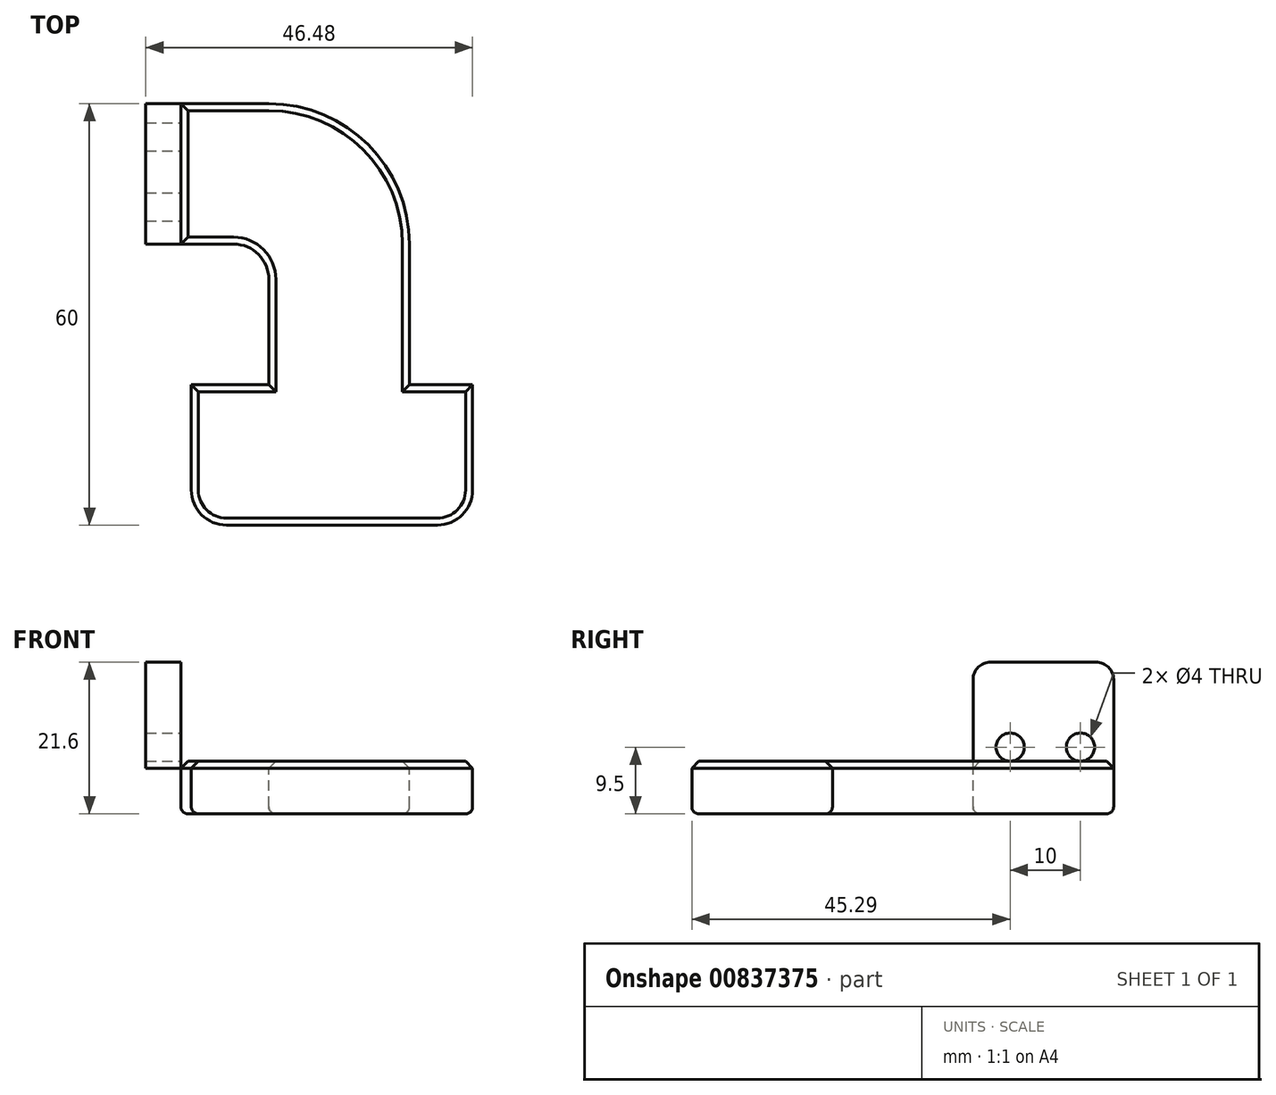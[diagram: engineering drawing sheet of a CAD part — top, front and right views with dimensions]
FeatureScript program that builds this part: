
annotation { "Feature Type Name" : "Feature", "Feature Type Description" : "" }
export const myFeature = defineFeature(function(context is Context, id is Id, definition is map)
    precondition{}
    {
        {
            var Q0;
            Q0=qCreatedBy(makeId("Top.planeOp"),FACE);
            var sketch = newSketch(context, id + "F0", { "sketchPlane" : qUnion([Q0])});
            skLineSegment(sketch, "E0.bottom", {"start": v(-27.76, 10) * mm, "end": v(-15.26, 10) * mm});
            skLineSegment(sketch, "E0.top", {"start": v(-27.76, -10) * mm, "end": v(-20.26, -10) * mm});
            skLineSegment(sketch, "E1.top", {"start": v(4.74, -30) * mm, "end": v(-15.26, -30) * mm});
            skLineSegment(sketch, "E1.left", {"start": v(4.74, -10) * mm, "end": v(4.74, -30) * mm});
            skLineSegment(sketch, "E1.right", {"start": v(-15.26, -15) * mm, "end": v(-15.26, -30) * mm});
            skLineSegment(sketch, "E2.bottom", {"start": v(13.72, -30) * mm, "end": v(-26.28, -30) * mm});
            skLineSegment(sketch, "E2.top", {"start": v(8.72, -50) * mm, "end": v(-21.28, -50) * mm});
            skLineSegment(sketch, "E2.left", {"start": v(13.72, -30) * mm, "end": v(13.72, -45) * mm});
            skLineSegment(sketch, "E2.right", {"start": v(-26.28, -30) * mm, "end": v(-26.28, -45) * mm});
            skPoint(sketch, "E3.visualSharp", {"position": v(4.74, 10) * mm});
            skArc(sketch, "E3.filletArc", {"start": v(4.74, -10) * mm, "mid": v(-1.12, 4.14) * mm, "end": v(-15.26, 10) * mm});
            skArc(sketch, "E4.filletArc", {"start": v(-15.26, -15) * mm, "mid": v(-16.72, -11.46) * mm, "end": v(-20.26, -10) * mm});
            skPoint(sketch, "E5.visualSharp", {"position": v(13.72, -50) * mm});
            skArc(sketch, "E5.filletArc", {"start": v(8.72, -50) * mm, "mid": v(12.26, -48.54) * mm, "end": v(13.72, -45) * mm});
            skPoint(sketch, "E6.visualSharp", {"position": v(-26.28, -50) * mm});
            skArc(sketch, "E6.filletArc", {"start": v(-26.28, -45) * mm, "mid": v(-24.81, -48.54) * mm, "end": v(-21.28, -50) * mm});
            skLineSegment(sketch, "E7.left", {"start": v(-27.76, 10) * mm, "end": v(-27.76, -10) * mm});
            skPoint(sketch, "E8.center.orphan", {"position": v(-40.26, 0) * mm});
            skPoint(sketch, "E9.orphan", {"position": v(-52.17, -10) * mm});
            skPoint(sketch, "E10.orphan", {"position": v(-40.26, 10) * mm});
            skPoint(sketch, "E11.orphan", {"position": v(-40.26, -10) * mm});
            skSolve(sketch);
        }
        {
            var Q0;
            Q0=makeQuery(id+"F0.imprint","IMPRINT",FACE,{"disambiguationData":[TD([[makeQuery(id+"F0.imprint","IMPRINT",EDGE,{"derivedFrom":sQuery(id+"F0.wireOp",EDGE,"E8")}),-1.0]])]});
            var Q1;
            Q1=makeQuery(id+"F0.imprint","IMPRINT",FACE,{"disambiguationData":[TD([[makeQuery(id+"F0.imprint","IMPRINT",EDGE,{"derivedFrom":sQuery(id+"F0.wireOp",EDGE,"E0.bottom")}),-1.0]])]});
            var Q2;
            {var subQ1=sQuery(id+"F0.wireOp",EDGE,"E1.top");Q2=makeQuery(id+"F0.imprint","IMPRINT",FACE,{"disambiguationData":[TD([[makeQuery(id+"F0.imprint","IMPRINT",EDGE,{"derivedFrom":subQ1}),1.0]])]});}
            extrude(context, id + "F1", {"entities" : qUnion([Q0, Q1, Q2]), "oppositeDirection" : true, "depth" : 7.5 * mm, "offsetDistance" : 25 * mm});
        }
        {
            var Q0;
            {var subQ1=sQuery(id+"F0.wireOp",EDGE,"E1.top");Q0=makeQuery(id+"F0.imprint","IMPRINT",FACE,{"disambiguationData":[TD([[makeQuery(id+"F0.imprint","IMPRINT",EDGE,{"derivedFrom":subQ1}),1.0]])]});}
            extrude(context, id + "F2", {"entities" : qUnion([Q0]), "operationType" : NewBodyOperationType.ADD, "oppositeDirection" : true, "depth" : 2.5 * mm, "offsetDistance" : 25 * mm});
        }
        {
            var Q0;
            Q0=makeQuery(id+"F1.opExtrude","CAP_EDGE",EDGE,{"disambiguationData":[OSD([sQuery(id+"F0.wireOp",EDGE,"E8")])],"isStart":false});
            var Q1;
            Q1=makeQuery(id+"F1.opExtrude","CAP_FACE",FACE,{"disambiguationData":[OSD([sQuery(id+"F0.wireOp",EDGE,"E0.bottom"),sQuery(id+"F0.wireOp",EDGE,"E0.top"),sQuery(id+"F0.wireOp",EDGE,"E1.left"),sQuery(id+"F0.wireOp",EDGE,"E1.right"),sQuery(id+"F0.wireOp",EDGE,"E2.bottom"),sQuery(id+"F0.wireOp",EDGE,"E2.top"),sQuery(id+"F0.wireOp",EDGE,"E2.left"),sQuery(id+"F0.wireOp",EDGE,"E2.right"),sQuery(id+"F0.wireOp",EDGE,"E3.filletArc"),sQuery(id+"F0.wireOp",EDGE,"E4.filletArc"),sQuery(id+"F0.wireOp",EDGE,"E5.filletArc"),sQuery(id+"F0.wireOp",EDGE,"E6.filletArc"),sQuery(id+"F0.wireOp",EDGE,"E7.left")])],"isStart":false});
            var Q2;
            {var subQ0=sQuery(id+"F0.wireOp",EDGE,"E2.bottom");Q2=makeQuery(id+"F2.boolean.opBoolean","SPLIT",EDGE,{"disambiguationData":[topologyDisambiguationEdgeConnected([makeQuery(id+"F1.opExtrude","SWEPT_FACE",FACE,{"disambiguationData":[OSD([subQ0])]}),makeQuery(id+"F2.opExtrude","CAP_FACE",FACE,{"disambiguationData":[OSD([subQ0,sQuery(id+"F0.wireOp",EDGE,"E2.top"),sQuery(id+"F0.wireOp",EDGE,"E2.left"),sQuery(id+"F0.wireOp",EDGE,"E2.right"),sQuery(id+"F0.wireOp",EDGE,"E5.filletArc"),sQuery(id+"F0.wireOp",EDGE,"E6.filletArc")])],"isStart":false})])],"derivedFrom":makeQuery(id+"F2.opExtrude","CAP_EDGE",EDGE,{"disambiguationData":[OSD([subQ0])],"isStart":false})});}
            fillet(context, id + "F3", {"entities" : qUnion([Q0, Q1, Q2]), "radius" : 1 * mm, "tangentPropagation" : true, "allowEdgeOverflow" : false});
        }
        {
            var Q0;
            Q0=makeQuery(id+"F1.opExtrude","CAP_FACE",FACE,{"disambiguationData":[OSD([sQuery(id+"F0.wireOp",EDGE,"E0.bottom"),sQuery(id+"F0.wireOp",EDGE,"E0.top"),sQuery(id+"F0.wireOp",EDGE,"E1.left"),sQuery(id+"F0.wireOp",EDGE,"E1.right"),sQuery(id+"F0.wireOp",EDGE,"E2.bottom"),sQuery(id+"F0.wireOp",EDGE,"E2.top"),sQuery(id+"F0.wireOp",EDGE,"E2.left"),sQuery(id+"F0.wireOp",EDGE,"E2.right"),sQuery(id+"F0.wireOp",EDGE,"E3.filletArc"),sQuery(id+"F0.wireOp",EDGE,"E4.filletArc"),sQuery(id+"F0.wireOp",EDGE,"E5.filletArc"),sQuery(id+"F0.wireOp",EDGE,"E6.filletArc"),sQuery(id+"F0.wireOp",EDGE,"E7.left")])],"isStart":true});
            chamfer(context, id + "F4", {"entities" : qUnion([Q0]), "width" : 1 * mm, "tangentPropagation" : true});
        }
        {
            var Q0;
            Q0=makeQuery(id+"F1.opExtrude","SWEPT_FACE",FACE,{"disambiguationData":[OSD([sQuery(id+"F0.wireOp",EDGE,"E7.left")])]});
            var sketch = newSketch(context, id + "F5", { "sketchPlane" : qUnion([Q0])});
            skLineSegment(sketch, "E12.right", {"start": v(-3.31, 2.29) * mm, "end": v(-3.29, 2) * mm});
            skLineSegment(sketch, "E13.bottom", {"start": v(-10, -1) * mm, "end": v(10, -1) * mm});
            skLineSegment(sketch, "E13.top", {"start": v(-7.5, 14.1) * mm, "end": v(7.5, 14.1) * mm});
            skLineSegment(sketch, "E13.left", {"start": v(-10, -1) * mm, "end": v(-10, 11.6) * mm});
            skLineSegment(sketch, "E13.right", {"start": v(10, -1) * mm, "end": v(10, 11.6) * mm});
            skArc(sketch, "E14", {"start": v(-3.29, 2) * mm, "mid": v(-3.3, 2.14) * mm, "end": v(-3.31, 2.29) * mm});
            skCircle(sketch, "E15", {"center": v(4.71, 2) * mm, "radius": 2 * mm});
            skCircle(sketch, "E16", {"center": v(-5.29, 2) * mm, "radius": 2 * mm});
            skPoint(sketch, "E17.center.orphan", {"position": v(-5.29, 4.4) * mm});
            skPoint(sketch, "E18.orphan", {"position": v(6.46, 2) * mm});
            skPoint(sketch, "E19.center.orphan", {"position": v(4.71, 4.4) * mm});
            skPoint(sketch, "E19.end.orphan", {"position": v(2.96, 4.4) * mm});
            skPoint(sketch, "E20.center.orphan", {"position": v(4.71, 9.6) * mm});
            skPoint(sketch, "E21.center.orphan", {"position": v(-5.29, 9.6) * mm});
            skPoint(sketch, "E22.visualSharp", {"position": v(-10, 14.1) * mm});
            skArc(sketch, "E22.filletArc", {"start": v(-7.5, 14.1) * mm, "mid": v(-9.27, 13.37) * mm, "end": v(-10, 11.6) * mm});
            skPoint(sketch, "E23.visualSharp", {"position": v(10, 14.1) * mm});
            skArc(sketch, "E23.filletArc", {"start": v(10, 11.6) * mm, "mid": v(9.27, 13.37) * mm, "end": v(7.5, 14.1) * mm});
            skSolve(sketch);
        }
        {
            var Q0;
            Q0=makeQuery(id+"F5.imprint","IMPRINT",FACE,{"disambiguationData":[TD([[makeQuery(id+"F5.imprint","IMPRINT",EDGE,{"derivedFrom":sQuery(id+"F5.wireOp",EDGE,"E13.top")}),-1.0]])]});
            extrude(context, id + "F6", {"entities" : qUnion([Q0]), "depth" : 5 * mm, "offsetDistance" : 25 * mm});
        }
    });
